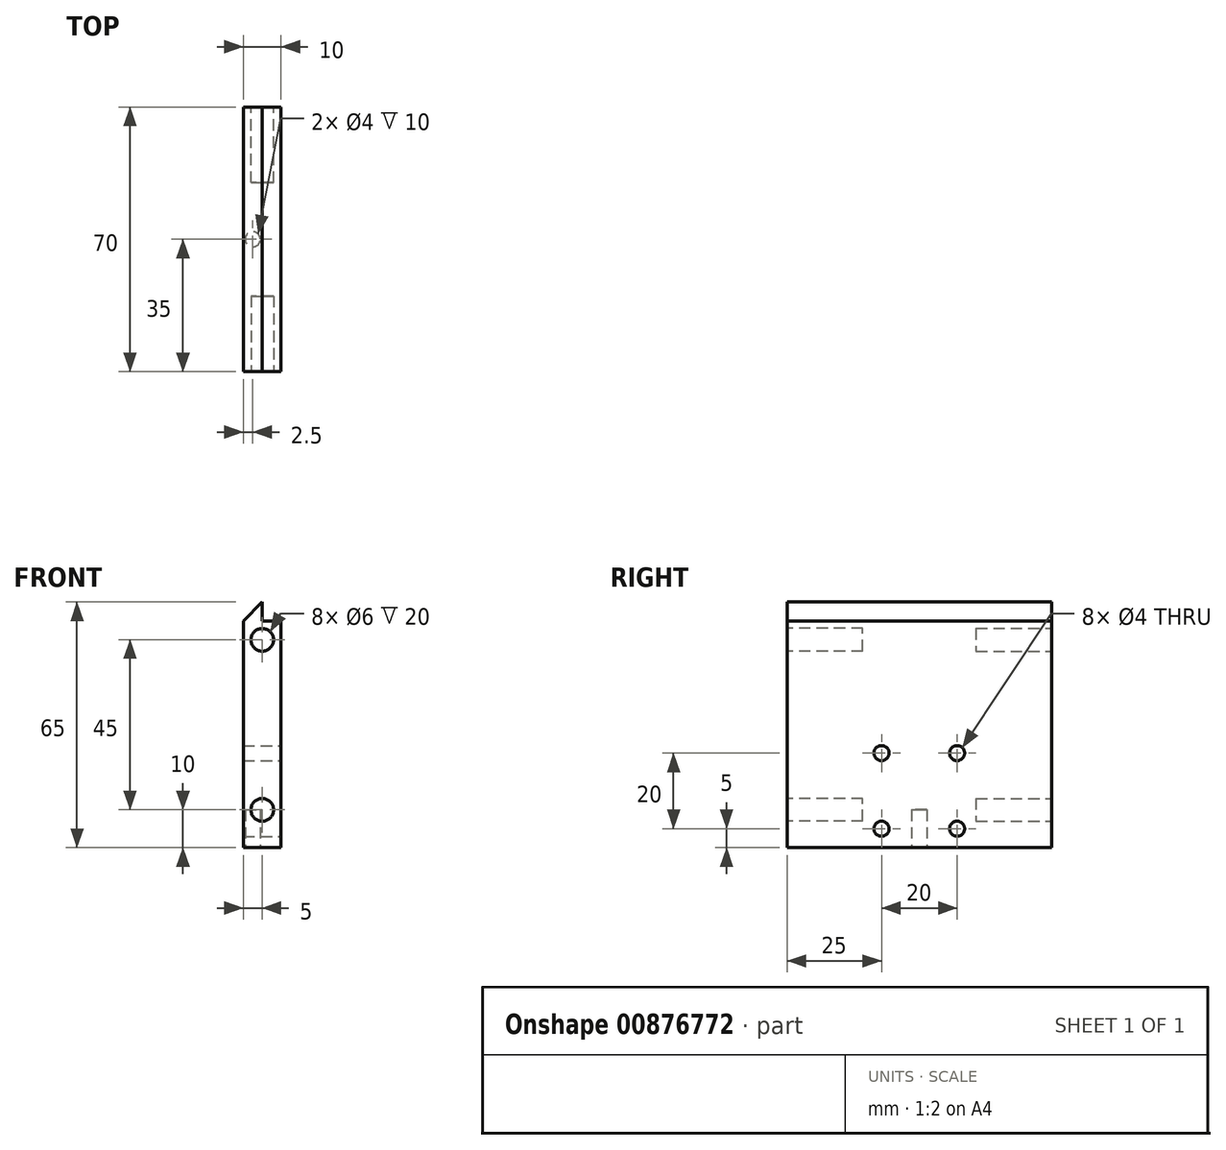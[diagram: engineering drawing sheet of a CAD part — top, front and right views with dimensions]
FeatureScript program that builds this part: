
annotation { "Feature Type Name" : "Feature", "Feature Type Description" : "" }
export const myFeature = defineFeature(function(context is Context, id is Id, definition is map)
    precondition{}
    {
        {
            var Q0;
            Q0=qCreatedBy(makeId("Front.planeOp"),FACE);
            var sketch = newSketch(context, id + "F0", { "sketchPlane" : qUnion([Q0])});
            skLineSegment(sketch, "E0.top", {"start": v(-5, -32.5) * mm, "end": v(5, -32.5) * mm});
            skLineSegment(sketch, "E0.left", {"start": v(-5, 27.5) * mm, "end": v(-5, -32.5) * mm});
            skLineSegment(sketch, "E0.right", {"start": v(5, 27.5) * mm, "end": v(5, -32.5) * mm});
            skPoint(sketch, "E0.middle", {"position": v(0, 0) * mm});
            skPoint(sketch, "E1", {"position": v(0, -22.5) * mm});
            skPoint(sketch, "E2", {"position": v(0, 22.5) * mm});
            skLineSegment(sketch, "E3", {"start": v(0, 32.5) * mm, "end": v(-5, 27.5) * mm});
            skLineSegment(sketch, "E4.top", {"start": v(0, 27.5) * mm, "end": v(5, 27.5) * mm});
            skLineSegment(sketch, "E4.left", {"start": v(0, 32.5) * mm, "end": v(0, 27.5) * mm});
            skSolve(sketch);
        }
        {
            var Q0;
            {var subQ1=sQuery(id+"F0.wireOp",EDGE,"E0.top");Q0=makeQuery(id+"F0.imprint","IMPRINT",FACE,{"disambiguationData":[TD([[makeQuery(id+"F0.imprint","IMPRINT",EDGE,{"derivedFrom":subQ1}),1.0]])]});}
            extrude(context, id + "F1", {"entities" : qUnion([Q0]), "depth" : 70 * mm, "offsetDistance" : 25 * mm});
        }
        {
            var Q0;
            Q0=makeQuery(id+"F1.opExtrude","SWEPT_FACE",FACE,{"disambiguationData":[OSD([sQuery(id+"F0.wireOp",EDGE,"E0.top")])]});
            var sketch = newSketch(context, id + "F2", { "sketchPlane" : qUnion([Q0])});
            skPoint(sketch, "E5.centerSnap0", {"position": v(-5, 35) * mm});
            skCircle(sketch, "E6", {"center": v(-2.5, 35) * mm, "radius": 2 * mm});
            skSolve(sketch);
        }
        {
            var Q0;
            Q0=makeQuery(id+"F1.opExtrude","SWEPT_FACE",FACE,{"disambiguationData":[OSD([sQuery(id+"F0.wireOp",EDGE,"E0.right")])]});
            var sketch = newSketch(context, id + "F3", { "sketchPlane" : qUnion([Q0])});
            skCircle(sketch, "E7", {"center": v(-45, -27.5) * mm, "radius": 2 * mm});
            skCircle(sketch, "E8", {"center": v(-45, -7.5) * mm, "radius": 2 * mm});
            skCircle(sketch, "E9", {"center": v(-25, -7.5) * mm, "radius": 2 * mm});
            skCircle(sketch, "E10", {"center": v(-25, -27.5) * mm, "radius": 2 * mm});
            skSolve(sketch);
        }
        {
            var Q0;
            Q0=qSketchRegion(id+"F3",true);
            extrude(context, id + "F4", {"entities" : qUnion([Q0]), "operationType" : NewBodyOperationType.REMOVE, "oppositeDirection" : true, "depth" : 25 * mm, "offsetDistance" : 25 * mm});
        }
        {
            var Q0;
            Q0=makeQuery(id+"F1.opExtrude","SWEPT_FACE",FACE,{"disambiguationData":[OSD([sQuery(id+"F0.wireOp",EDGE,"E0.top")])]});
            var sketch = newSketch(context, id + "F5", { "sketchPlane" : qUnion([Q0])});
            skSolve(sketch);
        }
        {
            var Q0;
            Q0=makeQuery(id+"F1.opExtrude","CAP_FACE",FACE,{"disambiguationData":[OSD([sQuery(id+"F0.wireOp",EDGE,"E0.top"),sQuery(id+"F0.wireOp",EDGE,"E0.left"),sQuery(id+"F0.wireOp",EDGE,"E0.right"),sQuery(id+"F0.wireOp",EDGE,"E3"),sQuery(id+"F0.wireOp",EDGE,"E4.top"),sQuery(id+"F0.wireOp",EDGE,"E4.left")])],"isStart":false});
            var sketch = newSketch(context, id + "F6", { "sketchPlane" : qUnion([Q0])});
            skCircle(sketch, "E11", {"center": v(0, -22.5) * mm, "radius": 3 * mm});
            skPoint(sketch, "E11.centerSnap0", {"position": v(0, -32.5) * mm});
            skSolve(sketch);
        }
        {
            var Q0;
            Q0=qSketchRegion(id+"F6",true);
            extrude(context, id + "F7", {"entities" : qUnion([Q0]), "operationType" : NewBodyOperationType.REMOVE, "oppositeDirection" : true, "depth" : 20 * mm, "offsetDistance" : 25 * mm});
        }
        {
            var Q0;
            Q0=makeQuery(id+"F1.opExtrude","CAP_FACE",FACE,{"disambiguationData":[OSD([sQuery(id+"F0.wireOp",EDGE,"E0.top"),sQuery(id+"F0.wireOp",EDGE,"E0.left"),sQuery(id+"F0.wireOp",EDGE,"E0.right"),sQuery(id+"F0.wireOp",EDGE,"E3"),sQuery(id+"F0.wireOp",EDGE,"E4.top"),sQuery(id+"F0.wireOp",EDGE,"E4.left")])],"isStart":false});
            var sketch = newSketch(context, id + "F8", { "sketchPlane" : qUnion([Q0])});
            skCircle(sketch, "E12", {"center": v(0, 22.5) * mm, "radius": 3 * mm});
            skSolve(sketch);
        }
        {
            var Q0;
            Q0=qSketchRegion(id+"F8",true);
            extrude(context, id + "F9", {"entities" : qUnion([Q0]), "operationType" : NewBodyOperationType.REMOVE, "oppositeDirection" : true, "depth" : 20 * mm, "offsetDistance" : 25 * mm});
        }
        {
            var Q0;
            Q0=makeQuery(id+"F1.opExtrude","CAP_FACE",FACE,{"disambiguationData":[OSD([sQuery(id+"F0.wireOp",EDGE,"E0.top"),sQuery(id+"F0.wireOp",EDGE,"E0.left"),sQuery(id+"F0.wireOp",EDGE,"E0.right"),sQuery(id+"F0.wireOp",EDGE,"E3"),sQuery(id+"F0.wireOp",EDGE,"E4.top"),sQuery(id+"F0.wireOp",EDGE,"E4.left")])],"isStart":true});
            var sketch = newSketch(context, id + "F10", { "sketchPlane" : qUnion([Q0])});
            skCircle(sketch, "E13", {"center": v(0, -22.5) * mm, "radius": 3 * mm});
            skPoint(sketch, "E13.centerSnap0", {"position": v(0, -32.5) * mm});
            skSolve(sketch);
        }
        {
            var Q0;
            Q0=qSketchRegion(id+"F10",true);
            extrude(context, id + "F11", {"entities" : qUnion([Q0]), "operationType" : NewBodyOperationType.REMOVE, "oppositeDirection" : true, "depth" : 20 * mm, "offsetDistance" : 25 * mm});
        }
        {
            var Q0;
            Q0=makeQuery(id+"F1.opExtrude","CAP_FACE",FACE,{"disambiguationData":[OSD([sQuery(id+"F0.wireOp",EDGE,"E0.top"),sQuery(id+"F0.wireOp",EDGE,"E0.left"),sQuery(id+"F0.wireOp",EDGE,"E0.right"),sQuery(id+"F0.wireOp",EDGE,"E3"),sQuery(id+"F0.wireOp",EDGE,"E4.top"),sQuery(id+"F0.wireOp",EDGE,"E4.left")])],"isStart":true});
            var sketch = newSketch(context, id + "F12", { "sketchPlane" : qUnion([Q0])});
            skCircle(sketch, "E14", {"center": v(0, 22.5) * mm, "radius": 3 * mm});
            skPoint(sketch, "E14.centerSnap0", {"position": v(0, -32.5) * mm});
            skSolve(sketch);
        }
        {
            var Q0;
            Q0=qSketchRegion(id+"F12",true);
            extrude(context, id + "F13", {"entities" : qUnion([Q0]), "operationType" : NewBodyOperationType.REMOVE, "oppositeDirection" : true, "depth" : 20 * mm, "offsetDistance" : 25 * mm});
        }
        {
            var Q0;
            Q0=qSketchRegion(id+"F2",true);
            extrude(context, id + "F14", {"entities" : qUnion([Q0]), "operationType" : NewBodyOperationType.REMOVE, "oppositeDirection" : true, "depth" : 10 * mm, "offsetDistance" : 25 * mm});
        }
        {
            var Q0;
            Q0 = qSketchRegion(id + "F3", true);
            extrude(context, id + "F15", {"entities" : qUnion([Q0]), "operationType" : NewBodyOperationType.REMOVE, "oppositeDirection" : true, "depth" : 25 * mm, "offsetDistance" : 25 * mm});
        }
    });
